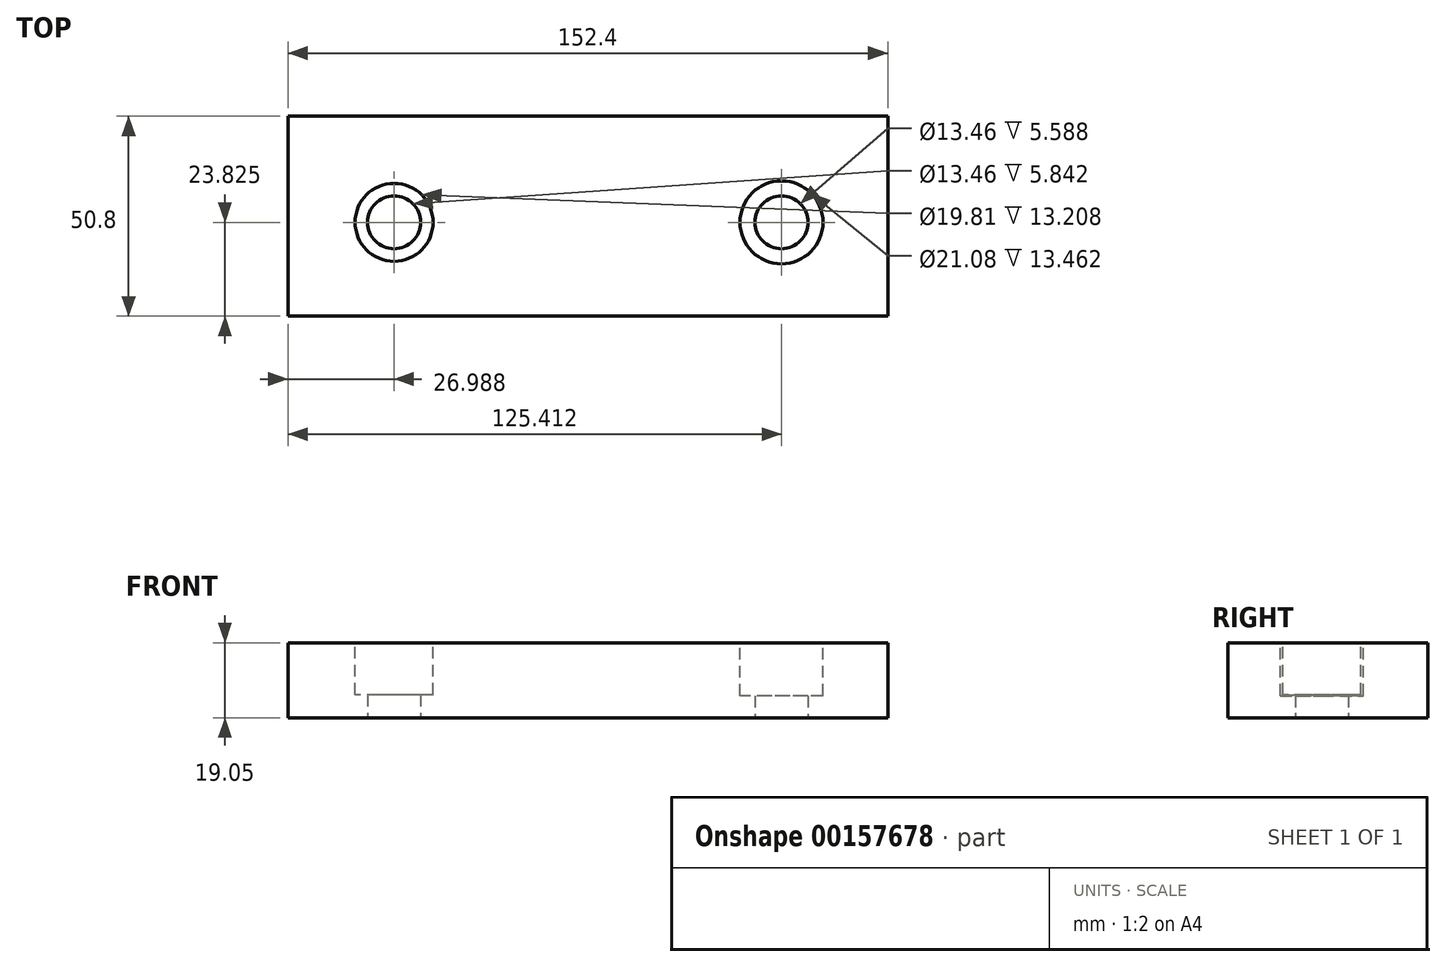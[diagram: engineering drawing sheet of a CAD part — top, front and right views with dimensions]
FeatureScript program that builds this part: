
annotation { "Feature Type Name" : "Feature", "Feature Type Description" : "" }
export const myFeature = defineFeature(function(context is Context, id is Id, definition is map)
    precondition{}
    {
        {
            var Q0;
            Q0=qCreatedBy(makeId("Top.planeOp"),FACE);
            var sketch = newSketch(context, id + "F0", { "sketchPlane" : qUnion([Q0])});
            skLineSegment(sketch, "E0.bottom", {"start": v(76.2, -25.4) * mm, "end": v(-76.2, -25.4) * mm});
            skLineSegment(sketch, "E0.top", {"start": v(76.2, 25.4) * mm, "end": v(-76.2, 25.4) * mm});
            skLineSegment(sketch, "E0.left", {"start": v(76.2, -25.4) * mm, "end": v(76.2, 25.4) * mm});
            skLineSegment(sketch, "E0.right", {"start": v(-76.2, -25.4) * mm, "end": v(-76.2, 25.4) * mm});
            skPoint(sketch, "E0.middle", {"position": v(0, 0) * mm});
            skCircle(sketch, "E1", {"center": v(-49.21, -1.57) * mm, "radius": 6.73 * mm});
            skCircle(sketch, "E2.1.0.0", {"center": v(49.21, -1.57) * mm, "radius": 6.73 * mm});
            skLineSegment(sketch, "E2.1.0.1", {"start": v(174.63, -25.4) * mm, "end": v(22.23, -25.4) * mm});
            skLineSegment(sketch, "E2.direction1", {"start": v(-49.21, -1.57) * mm, "end": v(49.21, -1.57) * mm, "construction": true});
            skSolve(sketch);
        }
        {
            var Q0;
            {var subQ1=sQuery(id+"F0.wireOp",EDGE,"E0.bottom");Q0=makeQuery(id+"F0.imprint","IMPRINT",FACE,{"disambiguationData":[TD([[makeQuery(id+"F0.imprint","IMPRINT",EDGE,{"derivedFrom":subQ1}),-1.0]])]});}
            extrude(context, id + "F1", {"entities" : qUnion([Q0]), "depth" : 19.05 * mm});
        }
        {
            var Q0;
            Q0=makeQuery(id+"F1.opExtrude","CAP_FACE",FACE,{"disambiguationData":[OSD([sQuery(id+"F0.wireOp",EDGE,"E0.bottom"),sQuery(id+"F0.wireOp",EDGE,"E0.top"),sQuery(id+"F0.wireOp",EDGE,"E0.left"),sQuery(id+"F0.wireOp",EDGE,"E0.right"),sQuery(id+"F0.wireOp",EDGE,"E1"),sQuery(id+"F0.wireOp",EDGE,"E2.1.0.0"),sQuery(id+"F0.wireOp",EDGE,"E2.1.0.1")])],"isStart":false});
            var sketch = newSketch(context, id + "F2", { "sketchPlane" : qUnion([Q0])});
            skCircle(sketch, "E3.0", {"center": v(-49.21, -1.57) * mm, "radius": 6.73 * mm});
            skCircle(sketch, "E3.1", {"center": v(49.21, -1.57) * mm, "radius": 6.73 * mm});
            skCircle(sketch, "E4", {"center": v(-49.21, -1.57) * mm, "radius": 9.9 * mm});
            skCircle(sketch, "E5", {"center": v(49.21, -1.57) * mm, "radius": 9.9 * mm});
            skSolve(sketch);
        }
        {
            var Q0;
            Q0=makeQuery(id+"F2.imprint","IMPRINT",FACE,{"disambiguationData":[TD([[makeQuery(id+"F2.imprint","IMPRINT",EDGE,{"derivedFrom":sQuery(id+"F2.wireOp",EDGE,"E3.0")}),-1.0]])]});
            var Q1;
            Q1=sQuery(id+"F2.wireOp",EDGE,"E4");
            extrude(context, id + "F3", {"entities" : qUnion([Q0]), "operationType" : NewBodyOperationType.REMOVE, "surfaceEntities" : qUnion([Q1]), "oppositeDirection" : true, "depth" : 13.2 * mm});
        }
        {
            var Q0;
            Q0=makeQuery(id+"F1.opExtrude","CAP_FACE",FACE,{"disambiguationData":[OSD([sQuery(id+"F0.wireOp",EDGE,"E0.bottom"),sQuery(id+"F0.wireOp",EDGE,"E0.top"),sQuery(id+"F0.wireOp",EDGE,"E0.left"),sQuery(id+"F0.wireOp",EDGE,"E0.right"),sQuery(id+"F0.wireOp",EDGE,"E1"),sQuery(id+"F0.wireOp",EDGE,"E2.1.0.0"),sQuery(id+"F0.wireOp",EDGE,"E2.1.0.1")])],"isStart":false});
            var sketch = newSketch(context, id + "F4", { "sketchPlane" : qUnion([Q0])});
            skCircle(sketch, "E6", {"center": v(49.21, -1.57) * mm, "radius": 10.54 * mm});
            skSolve(sketch);
        }
        {
            var Q0;
            Q0=makeQuery(id+"F4.imprint","IMPRINT",FACE,{"disambiguationData":[TD([[makeQuery(id+"F4.imprint","IMPRINT",EDGE,{"derivedFrom":sQuery(id+"F4.wireOp",EDGE,"E6")}),1.0]])]});
            var Q1;
            Q1=sQuery(id+"F4.wireOp",EDGE,"E6");
            extrude(context, id + "F5", {"entities" : qUnion([Q0]), "operationType" : NewBodyOperationType.REMOVE, "surfaceEntities" : qUnion([Q1]), "oppositeDirection" : true, "depth" : 13.46 * mm});
        }
    });
